# Revit family: MT-PROTILT AW-CA SGL GLZ SIDE LITE
name_source: partatom
category: Windows
revit_build: Autodesk Revit 2017 (Build: 20160225_1515(x64)
units: mm (PartAtom-declared; Revit-internal decimal feet)

## family parameters
Always vertical = Yes
Cut with Voids When Loaded = No
Host = Wall
OmniClass Number = 23.30.20.00
OmniClass Title = Windows
Room Calculation Point = No
Shared = No

## types (2) — shared parameters
ANZRC COMPLIANT = YES
BOT PANEL POSITION = 55 mm
DOUBLE GLAZED THICKNESS = 18 mm
Default Sill Height = 900 mm  [stored 2.95276 ft]
FRAME MATERIAL = <By Category>
FRAME THICKNESS = 102 mm
GLAZED MATERIAL = Glass
MAX HEIGHT = 2000 mm  [stored 6.56168 ft]
MAX PANEL HEIGHT = 2000 mm  [stored 6.56168 ft]
MAX PANEL WIDTH = 1500 mm  [stored 4.92126 ft]
MAX WIDTH = 1500 mm  [stored 4.92126 ft]
Manufacturer = ALSPEC
Model = HAWKESBURY TOP HUNG COMMERCIAL SLIDING DOOR
OFFSET = 10 mm  [stored 0.0328084 ft]
SINGLE GLAZED THICKNESS = 5 mm  [stored 0.0164042 ft]
URL = WWW.ALSPEC.COM.AU
VERSION = 2.1
WARNING = No
Wall Closure = By host
YEAR = 2019
zero-valued in all types: TOLERANCE

## per-type parameters (varying)
| type | GAP | Height | JAMB WIDTH | MIDDLE JAMB WIDTH | OVERALL FRAME HEIGHT | OVERALL FRAME WIDTH | PANEL HEIGHT | PANEL WIDTH | Rough Height | Rough Width | TRANSOM HEIGHT | TRANSOM WIDTH | Width |
| HUNTER EVO | 7 mm  [stored 0.0229659 ft] | 1500 mm  [stored 4.92126 ft] | 50 mm  [stored 0.164042 ft] | 26 mm  [stored 0.0853018 ft] | 1500 mm  [stored 4.92126 ft] | 1500 mm  [stored 4.92126 ft] | 1390 mm | 1410 mm  [stored 4.62598 ft] | 1500 mm  [stored 4.92126 ft] | 1500 mm  [stored 4.92126 ft] | 1500 mm  [stored 4.92126 ft] | 1500 mm  [stored 4.92126 ft] | 1500 mm  [stored 4.92126 ft] |
| MCARTHUR 101.6 | 5 mm  [stored 0.0164042 ft] | 1800 mm  [stored 5.90551 ft] | 44 mm | 23 mm  [stored 0.0754593 ft] | 1800 mm  [stored 5.90551 ft] | 1300 mm  [stored 4.26509 ft] | 1690 mm | 1223 mm | 1800 mm  [stored 5.90551 ft] | 1300 mm  [stored 4.26509 ft] | 1800 mm  [stored 5.90551 ft] | 1300 mm  [stored 4.26509 ft] | 1300 mm  [stored 4.26509 ft] |

type visibility flags: 2 boolean params named "<type name>" — each type sets only its own to Yes (folded from table)

note: [stored X ft] marks values corroborated as IEEE doubles in the binary element streams (Revit-internal decimal feet)

## geometry (parser evidence)
native form markers: Sweep x28
no freeform markers — native parametric forms only
